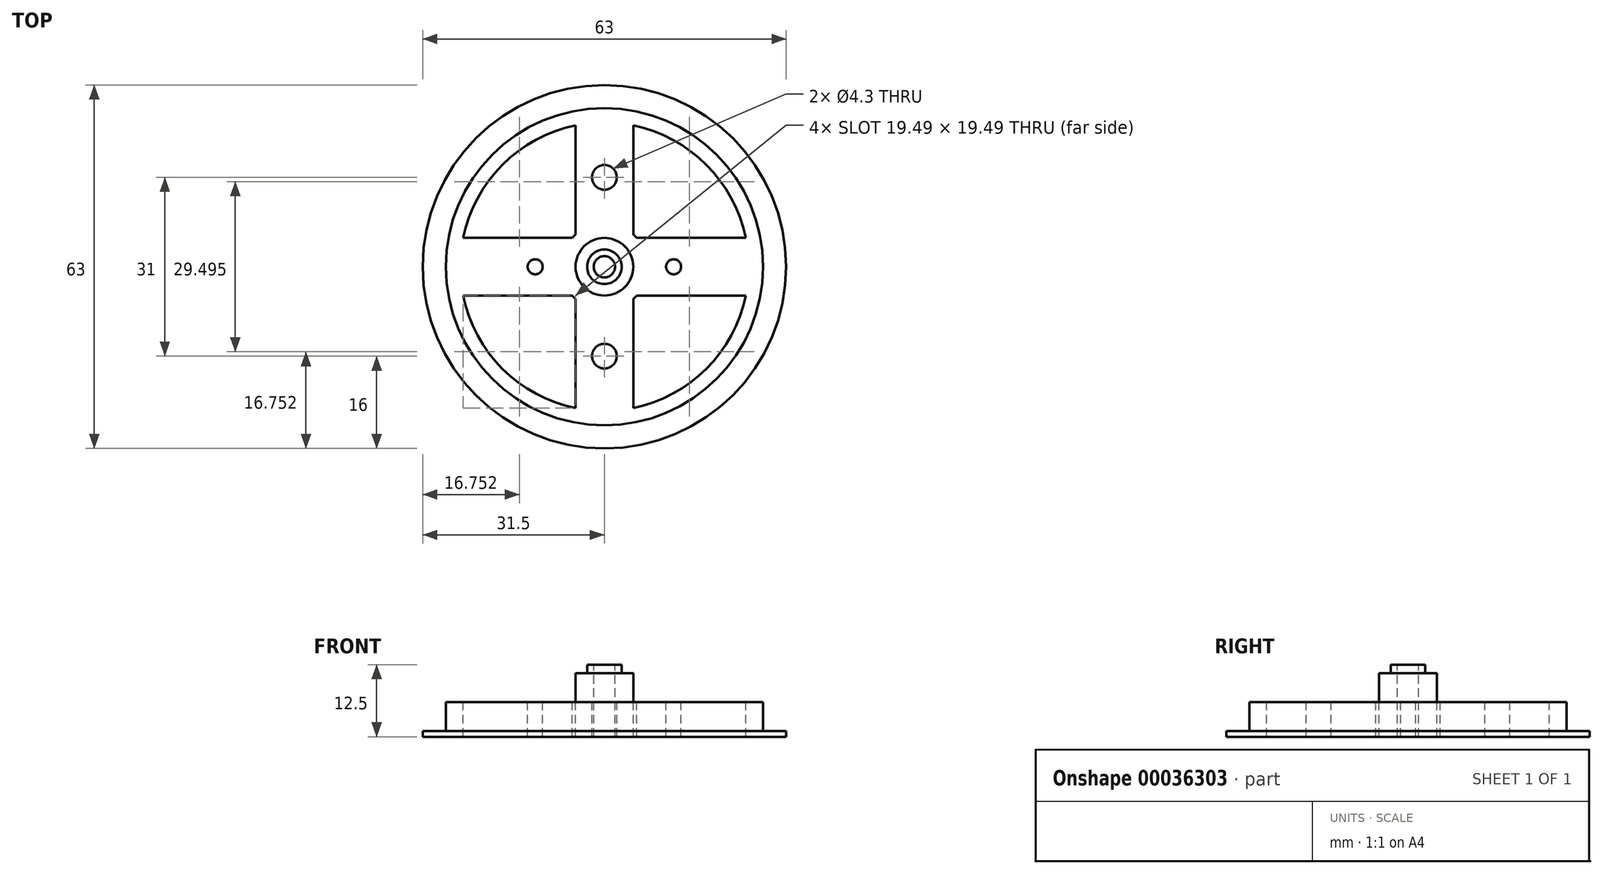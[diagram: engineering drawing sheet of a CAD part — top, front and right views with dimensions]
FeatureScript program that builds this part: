
annotation { "Feature Type Name" : "Feature", "Feature Type Description" : "" }
export const myFeature = defineFeature(function(context is Context, id is Id, definition is map)
    precondition{}
    {
        {
            var Q0;
            Q0=qCreatedBy(makeId("Top.planeOp"),FACE);
            var sketch = newSketch(context, id + "F0", { "sketchPlane" : qUnion([Q0])});
            skCircle(sketch, "E0", {"center": v(0, 0) * mm, "radius": 27.5 * mm});
            skSolve(sketch);
        }
        {
            var Q0;
            Q0=makeQuery(id+"F0.imprint","IMPRINT",FACE,{"disambiguationData":[TD([[makeQuery(id+"F0.imprint","IMPRINT",EDGE,{"derivedFrom":sQuery(id+"F0.wireOp",EDGE,"E0")}),1.0]])]});
            extrude(context, id + "F1", {"entities" : qUnion([Q0]), "depth" : 5 * mm});
        }
        {
            var Q0;
            Q0=makeQuery(id+"F1.opExtrude","CAP_FACE",FACE,{"disambiguationData":[OSD([sQuery(id+"F0.wireOp",EDGE,"E0")])],"isStart":false});
            var sketch = newSketch(context, id + "F2", { "sketchPlane" : qUnion([Q0])});
            skCircle(sketch, "E1", {"center": v(0, 0) * mm, "radius": 5 * mm});
            skSolve(sketch);
        }
        {
            var Q0;
            Q0=makeQuery(id+"F2.imprint","IMPRINT",FACE,{"disambiguationData":[TD([[makeQuery(id+"F2.imprint","IMPRINT",EDGE,{"derivedFrom":sQuery(id+"F2.wireOp",EDGE,"E1")}),1.0]])]});
            extrude(context, id + "F3", {"entities" : qUnion([Q0]), "operationType" : NewBodyOperationType.ADD, "depth" : 5 * mm});
        }
        {
            var Q0;
            Q0=makeQuery(id+"F3.opExtrude","CAP_FACE",FACE,{"disambiguationData":[OSD([sQuery(id+"F2.wireOp",EDGE,"E1")])],"isStart":false});
            var sketch = newSketch(context, id + "F4", { "sketchPlane" : qUnion([Q0])});
            skCircle(sketch, "E2", {"center": v(0, 0) * mm, "radius": 1.85 * mm});
            skSolve(sketch);
        }
        {
            var Q0;
            Q0=qSketchRegion(id+"F4",true);
            extrude(context, id + "F5", {"entities" : qUnion([Q0]), "operationType" : NewBodyOperationType.REMOVE, "endBound" : BoundingType.UP_TO_NEXT, "oppositeDirection" : true, "depth" : 25 * mm});
        }
        {
            var Q0;
            Q0=makeQuery(id+"F3.opExtrude","CAP_FACE",FACE,{"disambiguationData":[OSD([sQuery(id+"F2.wireOp",EDGE,"E1")])],"isStart":false});
            var sketch = newSketch(context, id + "F6", { "sketchPlane" : qUnion([Q0])});
            skCircle(sketch, "E3", {"center": v(0, 0) * mm, "radius": 3 * mm});
            skSolve(sketch);
        }
        {
            var Q0;
            Q0=makeQuery(id+"F6.imprint","IMPRINT",FACE,{"disambiguationData":[TD([[makeQuery(id+"F6.imprint","IMPRINT",EDGE,{"derivedFrom":sQuery(id+"F6.wireOp",EDGE,"E3")}),1.0]])]});
            extrude(context, id + "F7", {"entities" : qUnion([Q0]), "operationType" : NewBodyOperationType.ADD, "depth" : 1.5 * mm});
        }
        {
            var Q0;
            Q0=makeQuery(id+"F1.opExtrude","CAP_FACE",FACE,{"disambiguationData":[OSD([sQuery(id+"F0.wireOp",EDGE,"E0")])],"isStart":false});
            var sketch = newSketch(context, id + "F8", { "sketchPlane" : qUnion([Q0])});
            skCircle(sketch, "E4", {"center": v(0, 0) * mm, "radius": 25 * mm});
            skCircle(sketch, "E5", {"center": v(0, 0) * mm, "radius": 7.5 * mm});
            skLineSegment(sketch, "E6", {"start": v(0, -7.5) * mm, "end": v(0, -25) * mm, "construction": true});
            skLineSegment(sketch, "E7", {"start": v(-7.5, 0) * mm, "end": v(-25, 0) * mm, "construction": true});
            skLineSegment(sketch, "E8", {"start": v(0, 7.5) * mm, "end": v(0, 25) * mm, "construction": true});
            skLineSegment(sketch, "E9", {"start": v(7.5, 0) * mm, "end": v(25, 0) * mm, "construction": true});
            skLineSegment(sketch, "E10.0", {"start": v(5, 5.6) * mm, "end": v(5, 24.5) * mm});
            skLineSegment(sketch, "E11.0", {"start": v(-5, 5.6) * mm, "end": v(-5, 24.5) * mm});
            skLineSegment(sketch, "E12", {"start": v(5, -5.6) * mm, "end": v(5, -24.5) * mm});
            skLineSegment(sketch, "E13", {"start": v(-5, -5.6) * mm, "end": v(-5, -24.5) * mm});
            skLineSegment(sketch, "E14.0", {"start": v(5.6, 5) * mm, "end": v(24.5, 5) * mm});
            skLineSegment(sketch, "E15.0", {"start": v(5.6, -5) * mm, "end": v(24.5, -5) * mm});
            skLineSegment(sketch, "E16", {"start": v(-5.6, 5) * mm, "end": v(-24.5, 5) * mm});
            skLineSegment(sketch, "E17", {"start": v(-5.6, -5) * mm, "end": v(-24.5, -5) * mm});
            skCircle(sketch, "E18", {"center": v(-12, 0) * mm, "radius": 1.3 * mm});
            skCircle(sketch, "E19", {"center": v(12, 0) * mm, "radius": 1.3 * mm});
            skCircle(sketch, "E20", {"center": v(0, 15.5) * mm, "radius": 2.15 * mm});
            skCircle(sketch, "E21", {"center": v(0, -15.5) * mm, "radius": 2.15 * mm});
            skSolve(sketch);
        }
        {
            var Q0;
            {var subQ1=sQuery(id+"F8.wireOp",EDGE,"E10.0");Q0=makeQuery(id+"F8.imprint","IMPRINT",FACE,{"disambiguationData":[TD([[makeQuery(id+"F8.imprint","IMPRINT",EDGE,{"derivedFrom":subQ1}),-1.0]])]});}
            var Q1;
            {var subQ2=sQuery(id+"F8.wireOp",EDGE,"E11.0");Q1=makeQuery(id+"F8.imprint","IMPRINT",FACE,{"disambiguationData":[TD([[makeQuery(id+"F8.imprint","IMPRINT",EDGE,{"derivedFrom":subQ2}),1.0]])]});}
            var Q2;
            {var subQ1=sQuery(id+"F8.wireOp",EDGE,"E13");Q2=makeQuery(id+"F8.imprint","IMPRINT",FACE,{"disambiguationData":[TD([[makeQuery(id+"F8.imprint","IMPRINT",EDGE,{"derivedFrom":subQ1}),-1.0]])]});}
            var Q3;
            {var subQ0=sQuery(id+"F8.wireOp",EDGE,"E12");Q3=makeQuery(id+"F8.imprint","IMPRINT",FACE,{"disambiguationData":[TD([[makeQuery(id+"F8.imprint","IMPRINT",EDGE,{"derivedFrom":subQ0}),1.0]])]});}
            extrude(context, id + "F9", {"entities" : qUnion([Q0, Q1, Q2, Q3]), "operationType" : NewBodyOperationType.REMOVE, "endBound" : BoundingType.UP_TO_NEXT, "oppositeDirection" : true, "depth" : 25 * mm});
        }
        {
            var Q0;
            Q0=makeQuery(id+"F1.opExtrude","CAP_FACE",FACE,{"disambiguationData":[OSD([sQuery(id+"F0.wireOp",EDGE,"E0")])],"isStart":true});
            var sketch = newSketch(context, id + "F10", { "sketchPlane" : qUnion([Q0])});
            skCircle(sketch, "E22", {"center": v(0, 0) * mm, "radius": 31.5 * mm});
            skSolve(sketch);
        }
        {
            var Q0;
            Q0=makeQuery(id+"F10.imprint","IMPRINT",FACE,{"disambiguationData":[TD([[makeQuery(id+"F10.imprint","IMPRINT",EDGE,{"derivedFrom":sQuery(id+"F10.wireOp",EDGE,"E22")}),1.0]])]});
            var Q1;
            {var subQ0=sQuery(id+"F0.wireOp",EDGE,"E0");Q1=makeQuery(id+"F10.imprint","IMPRINT",FACE,{"disambiguationData":[TD([[makeQuery(id+"F10.imprint","IMPRINT",EDGE,{"derivedFrom":makeQuery(id+"F1.opExtrude","CAP_EDGE",EDGE,{"disambiguationData":[OSD([subQ0])],"isStart":true})}),-1.0]])]});}
            extrude(context, id + "F11", {"entities" : qUnion([Q0, Q1]), "operationType" : NewBodyOperationType.ADD, "depth" : 1 * mm});
        }
        {
            var Q0;
            Q0=makeQuery(id+"F8.imprint","IMPRINT",FACE,{"disambiguationData":[TD([[makeQuery(id+"F8.imprint","IMPRINT",EDGE,{"derivedFrom":sQuery(id+"F8.wireOp",EDGE,"E18")}),1.0]])]});
            var Q1;
            Q1=makeQuery(id+"F8.imprint","IMPRINT",FACE,{"disambiguationData":[TD([[makeQuery(id+"F8.imprint","IMPRINT",EDGE,{"derivedFrom":sQuery(id+"F8.wireOp",EDGE,"E21")}),1.0]])]});
            var Q2;
            Q2=makeQuery(id+"F8.imprint","IMPRINT",FACE,{"disambiguationData":[TD([[makeQuery(id+"F8.imprint","IMPRINT",EDGE,{"derivedFrom":sQuery(id+"F8.wireOp",EDGE,"E19")}),1.0]])]});
            var Q3;
            Q3=makeQuery(id+"F8.imprint","IMPRINT",FACE,{"disambiguationData":[TD([[makeQuery(id+"F8.imprint","IMPRINT",EDGE,{"derivedFrom":sQuery(id+"F8.wireOp",EDGE,"E20")}),1.0]])]});
            extrude(context, id + "F12", {"entities" : qUnion([Q0, Q1, Q2, Q3]), "operationType" : NewBodyOperationType.REMOVE, "endBound" : BoundingType.UP_TO_NEXT, "oppositeDirection" : true, "depth" : 25 * mm});
        }
    });
